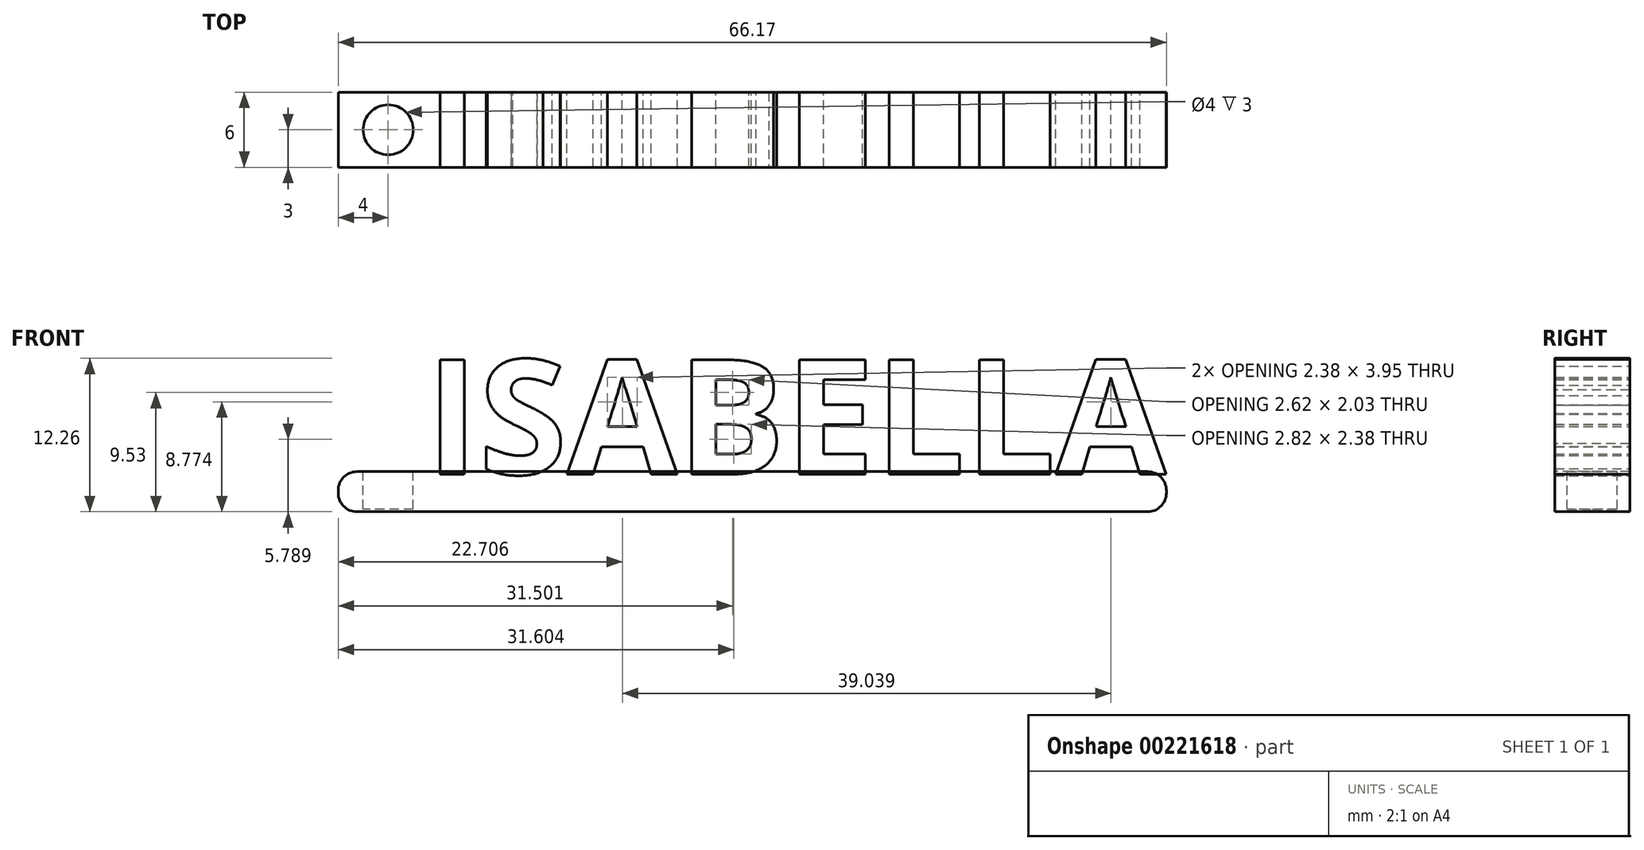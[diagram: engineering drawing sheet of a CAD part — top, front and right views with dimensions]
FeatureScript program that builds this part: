
annotation { "Feature Type Name" : "Feature", "Feature Type Description" : "" }
export const myFeature = defineFeature(function(context is Context, id is Id, definition is map)
    precondition{}
    {
        {
            var Q0;
            Q0=qCreatedBy(makeId("Front.planeOp"),FACE);
            var sketch = newSketch(context, id + "F0", { "sketchPlane" : qUnion([Q0])});
            skText(sketch, "E0", { "text": "ISABELLA", "fontName": "OpenSans-Bold.ttf"});
            const initialGuessF0  = {"E0": [-0.02, 0, 1, 0, 0.00921]};
            skSetInitialGuess(sketch, initialGuessF0);
            skSolve(sketch);
        }
        {
            var Q0;
            Q0=qCreatedBy(makeId("Top.planeOp"),FACE);
            var sketch = newSketch(context, id + "F1", { "sketchPlane" : qUnion([Q0])});
            skLineSegment(sketch, "E1.bottom", {"start": v(-20, 3) * mm, "end": v(39.17, 3) * mm});
            skLineSegment(sketch, "E1.top", {"start": v(-20, -3) * mm, "end": v(39.17, -3) * mm});
            skLineSegment(sketch, "E1.left", {"start": v(-20, 3) * mm, "end": v(-20, -3) * mm});
            skLineSegment(sketch, "E1.right", {"start": v(39.17, 3) * mm, "end": v(39.17, -3) * mm});
            skSolve(sketch);
        }
        {
            var Q0;
            Q0=qSketchRegion(id+"F0",true);
            extrude(context, id + "F2", {"entities" : qUnion([Q0]), "endBound" : BoundingType.SYMMETRIC, "depth" : 6 * mm});
        }
        {
            var Q0;
            Q0=makeQuery(id+"F1.imprint","IMPRINT",FACE,{"disambiguationData":[TD([[makeQuery(id+"F1.imprint","IMPRINT",EDGE,{"derivedFrom":sQuery(id+"F1.wireOp",EDGE,"E1.bottom")}),-1.0]])]});
            extrude(context, id + "F3", {"entities" : qUnion([Q0]), "depth" : 0.2 * mm});
        }
        {
            var Q0;
            Q0=makeQuery(id+"F3.opExtrude","CAP_FACE",FACE,{"disambiguationData":[OSD([sQuery(id+"F1.wireOp",EDGE,"E1.bottom"),sQuery(id+"F1.wireOp",EDGE,"E1.top"),sQuery(id+"F1.wireOp",EDGE,"E1.left"),sQuery(id+"F1.wireOp",EDGE,"E1.right")])],"isStart":true});
            extrude(context, id + "F4", {"entities" : qUnion([Q0]), "depth" : 3 * mm});
        }
        {
            var Q0;
            {var subQ0=sQuery(id+"F1.wireOp",EDGE,"E1.left");Q0=makeQuery(id+"FaVoHrOpcFZXiYX_6.opBoolean","MERGE",FACE,{"derivedFrom":[makeQuery(id+"F3.opExtrude","SWEPT_FACE",FACE,{"disambiguationData":[OSD([subQ0])]}),makeQuery(id+"F4.opExtrude","SWEPT_FACE",FACE,{"disambiguationData":[OSD([subQ0])]})]});}
            var sketch = newSketch(context, id + "F5", { "sketchPlane" : qUnion([Q0])});
            skLineSegment(sketch, "E2.bottom", {"start": v(-3, -3) * mm, "end": v(3, -3) * mm});
            skLineSegment(sketch, "E2.top", {"start": v(-3, 0.2) * mm, "end": v(3, 0.2) * mm});
            skLineSegment(sketch, "E2.left", {"start": v(-3, -3) * mm, "end": v(-3, 0.2) * mm});
            skLineSegment(sketch, "E2.right", {"start": v(3, -3) * mm, "end": v(3, 0.2) * mm});
            skSolve(sketch);
        }
        {
            var Q0;
            Q0=qSketchRegion(id+"F5",true);
            extrude(context, id + "F6", {"entities" : qUnion([Q0]), "operationType" : NewBodyOperationType.ADD, "depth" : 7 * mm});
        }
        {
            var Q0;
            Q0=makeQuery(id+"F6.opExtrude","CAP_EDGE",EDGE,{"disambiguationData":[OSD([sQuery(id+"F5.wireOp",EDGE,"E2.bottom")])],"isStart":false});
            var Q1;
            Q1=makeQuery(id+"F6.opExtrude","CAP_EDGE",EDGE,{"disambiguationData":[OSD([sQuery(id+"F5.wireOp",EDGE,"E2.top")])],"isStart":false});
            var Q2;
            Q2=makeQuery(id+"F4.opExtrude","CAP_EDGE",EDGE,{"disambiguationData":[OSD([sQuery(id+"F1.wireOp",EDGE,"E1.right")])],"isStart":false});
            var Q3;
            Q3=makeQuery(id+"F3.opExtrude","CAP_EDGE",EDGE,{"disambiguationData":[OSD([sQuery(id+"F1.wireOp",EDGE,"E1.right")])],"isStart":false});
            fillet(context, id + "F7", {"entities" : qUnion([Q0, Q1, Q2, Q3]), "radius" : 1.5 * mm, "tangentPropagation" : true, "allowEdgeOverflow" : false});
        }
        {
            var Q0;
            {var subQ19=sQuery(id+"F1.wireOp",EDGE,"E1.top");var subQ20=sQuery(id+"F1.wireOp",EDGE,"E1.bottom");var subQ63=sQuery(id+"F0.wireOp",EDGE,"E0.sketch_text.stroke-2");var subQ66=sQuery(id+"F1.wireOp",EDGE,"E1.left");Q0=makeQuery(id+"F6.boolean.opBoolean","MERGE",FACE,{"derivedFrom":[makeQuery(id+"FaVoHrOpcFZXiYX_6.opBoolean","SPLIT",FACE,{"disambiguationData":[TD([makeQuery(id+"F2.opExtrude","SWEPT_FACE",FACE,{"disambiguationData":[OSD([subQ63])]})])],"derivedFrom":makeQuery(id+"F3.opExtrude","CAP_FACE",FACE,{"disambiguationData":[OSD([subQ20,subQ19,subQ66,sQuery(id+"F1.wireOp",EDGE,"E1.right")])],"isStart":false})}),makeQuery(id+"F6.opExtrude","SWEPT_FACE",FACE,{"disambiguationData":[OSD([sQuery(id+"F5.wireOp",EDGE,"E2.top")])]})]});}
            var sketch = newSketch(context, id + "F8", { "sketchPlane" : qUnion([Q0])});
            skCircle(sketch, "E3", {"center": v(-23, 0) * mm, "radius": 2 * mm});
            skSolve(sketch);
        }
        {
            var Q0;
            Q0=makeQuery(id+"F8.imprint","IMPRINT",FACE,{"disambiguationData":[TD([[makeQuery(id+"F8.imprint","IMPRINT",EDGE,{"derivedFrom":sQuery(id+"F8.wireOp",EDGE,"E3")}),1.0]])]});
            extrude(context, id + "F9", {"entities" : qUnion([Q0]), "operationType" : NewBodyOperationType.REMOVE, "oppositeDirection" : true, "depth" : 3 * mm});
        }
    });
